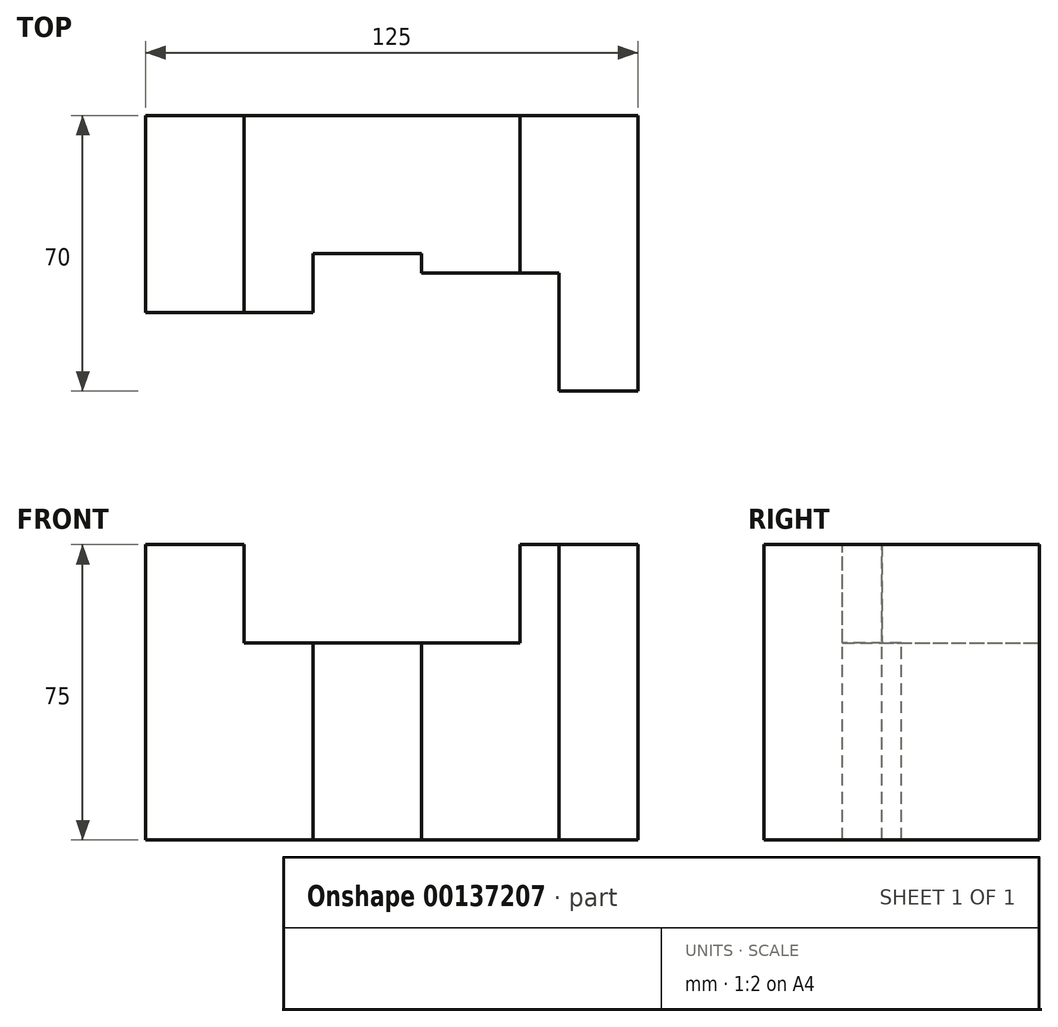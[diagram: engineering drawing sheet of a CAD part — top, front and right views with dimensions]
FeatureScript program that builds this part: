
annotation { "Feature Type Name" : "Feature", "Feature Type Description" : "" }
export const myFeature = defineFeature(function(context is Context, id is Id, definition is map)
    precondition{}
    {
        {
            var Q0;
            Q0=qCreatedBy(makeId("Front.planeOp"),FACE);
            var sketch = newSketch(context, id + "F0", { "sketchPlane" : qUnion([Q0])});
            skLineSegment(sketch, "E0", {"start": v(0, 0) * mm, "end": v(125, 0) * mm});
            skLineSegment(sketch, "E1", {"start": v(125, 0) * mm, "end": v(125, 75) * mm});
            skLineSegment(sketch, "E2", {"start": v(125, 75) * mm, "end": v(95, 75) * mm});
            skLineSegment(sketch, "E3", {"start": v(95, 75) * mm, "end": v(95, 50) * mm});
            skLineSegment(sketch, "E4", {"start": v(95, 50) * mm, "end": v(25, 50) * mm});
            skLineSegment(sketch, "E5", {"start": v(25, 50) * mm, "end": v(25, 75) * mm});
            skLineSegment(sketch, "E6", {"start": v(25, 75) * mm, "end": v(0, 75) * mm});
            skLineSegment(sketch, "E7", {"start": v(0, 75) * mm, "end": v(0, 0) * mm});
            skSolve(sketch);
        }
        {
            var Q0;
            Q0 = qSketchRegion(id + "F0", true);
            extrude(context, id + "F1", {"entities" : qUnion([Q0]), "depth" : 70 * mm});
        }
        {
            var Q0;
            Q0=makeQuery(id+"F1.opExtrude","SWEPT_FACE",FACE,{"disambiguationData":[OSD([sQuery(id+"F0.wireOp",EDGE,"E6")])]});
            var sketch = newSketch(context, id + "F2", { "sketchPlane" : qUnion([Q0])});
            skLineSegment(sketch, "E8", {"start": v(0, 0) * mm, "end": v(125, 0) * mm});
            skLineSegment(sketch, "E9", {"start": v(125, 0) * mm, "end": v(125, -70) * mm});
            skLineSegment(sketch, "E10", {"start": v(125, -70) * mm, "end": v(95, -70) * mm});
            skLineSegment(sketch, "E11", {"start": v(95, -70) * mm, "end": v(95, -40) * mm});
            skLineSegment(sketch, "E12", {"start": v(95, -40) * mm, "end": v(70, -40) * mm});
            skLineSegment(sketch, "E13", {"start": v(70, -40) * mm, "end": v(70, -35) * mm});
            skLineSegment(sketch, "E14", {"start": v(70, -35) * mm, "end": v(42.5, -35) * mm});
            skLineSegment(sketch, "E15", {"start": v(42.5, -35) * mm, "end": v(42.5, -50) * mm});
            skLineSegment(sketch, "E16", {"start": v(42.5, -50) * mm, "end": v(0, -50) * mm});
            skLineSegment(sketch, "E17", {"start": v(0, -50) * mm, "end": v(0, 0) * mm});
            skSolve(sketch);
        }
        {
            var Q0;
            {var subQ4=sQuery(id+"F2.wireOp",EDGE,"E17");Q0=makeQuery(id+"F2.imprint","IMPRINT",FACE,{"disambiguationData":[TD([[makeQuery(id+"F2.imprint","IMPRINT",EDGE,{"derivedFrom":subQ4}),-1.0]])]});}
            var sketch = newSketch(context, id + "F3", { "sketchPlane" : qUnion([Q0])});
            skLineSegment(sketch, "E18", {"start": v(0, -50) * mm, "end": v(42.5, -50) * mm});
            skLineSegment(sketch, "E19", {"start": v(42.5, -50) * mm, "end": v(42.5, -35) * mm});
            skLineSegment(sketch, "E20", {"start": v(42.5, -35) * mm, "end": v(70, -35) * mm});
            skLineSegment(sketch, "E21", {"start": v(70, -35) * mm, "end": v(70, -40) * mm});
            skLineSegment(sketch, "E22", {"start": v(70, -40) * mm, "end": v(105, -40) * mm});
            skLineSegment(sketch, "E23", {"start": v(105, -40) * mm, "end": v(105, -70) * mm});
            skLineSegment(sketch, "E24", {"start": v(105, -70) * mm, "end": v(0, -70) * mm});
            skLineSegment(sketch, "E25", {"start": v(0, -70) * mm, "end": v(0, -50) * mm});
            skSolve(sketch);
        }
        {
            var Q0;
            Q0 = qSketchRegion(id + "F3", true);
            extrude(context, id + "F4", {"entities" : qUnion([Q0]), "operationType" : NewBodyOperationType.REMOVE, "endBound" : BoundingType.THROUGH_ALL, "oppositeDirection" : true, "depth" : 25 * mm});
        }
    });
